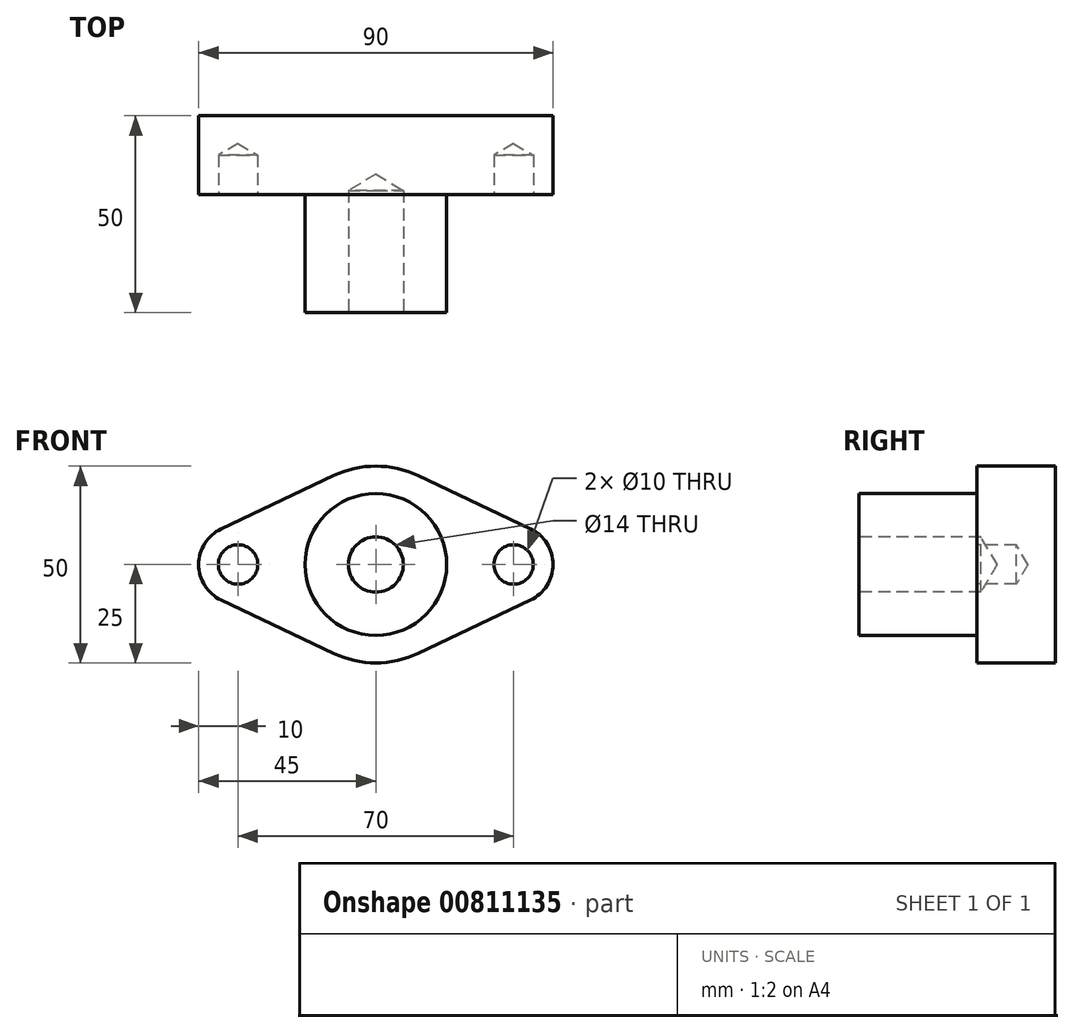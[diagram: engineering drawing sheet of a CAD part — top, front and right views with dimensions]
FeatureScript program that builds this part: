
annotation { "Feature Type Name" : "Feature", "Feature Type Description" : "" }
export const myFeature = defineFeature(function(context is Context, id is Id, definition is map)
    precondition{}
    {
        {
            var Q0;
            Q0=qCreatedBy(makeId("Front.planeOp"),FACE);
            var sketch = newSketch(context, id + "F0", { "sketchPlane" : qUnion([Q0])});
            skCircle(sketch, "E0", {"center": v(0, 0) * mm, "radius": 25 * mm});
            skPoint(sketch, "E1", {"position": v(-35, 0) * mm});
            skPoint(sketch, "E2", {"position": v(35, 0) * mm});
            skCircle(sketch, "E3", {"center": v(-35, 0) * mm, "radius": 10 * mm});
            skCircle(sketch, "E4", {"center": v(35, 0) * mm, "radius": 10 * mm});
            skLineSegment(sketch, "E5", {"start": v(-58.33, 0) * mm, "end": v(0, 27.67) * mm});
            skLineSegment(sketch, "E6", {"start": v(-58.33, 0) * mm, "end": v(0, -27.67) * mm});
            skLineSegment(sketch, "E7", {"start": v(58.33, 0) * mm, "end": v(0, -27.67) * mm});
            skLineSegment(sketch, "E8", {"start": v(0, 27.67) * mm, "end": v(58.33, 0) * mm});
            skSolve(sketch);
        }
        {
            var Q0;
            {var subQ0=sQuery(id+"F0.wireOp",EDGE,"E0");var subQ4=makeQuery(id+"F0.imprint","INTERSECT",VERTEX,{"derivedFrom":[subQ0,sQuery(id+"F0.wireOp",EDGE,"E8")]});Q0=makeQuery(id+"F0.imprint","IMPRINT",FACE,{"disambiguationData":[TD([[makeQuery(id+"F0.imprint","IMPRINT",EDGE,{"disambiguationData":[TD([[subQ4,1.0]])],"derivedFrom":subQ0}),1.0]])]});}
            var Q1;
            {var subQ0=sQuery(id+"F0.wireOp",EDGE,"E5");var subQ1=sQuery(id+"F0.wireOp",EDGE,"E3");var subQ2=makeQuery(id+"F0.imprint","INTERSECT",VERTEX,{"derivedFrom":[subQ1,subQ0]});Q1=makeQuery(id+"F0.imprint","IMPRINT",FACE,{"disambiguationData":[TD([[makeQuery(id+"F0.imprint","IMPRINT",EDGE,{"disambiguationData":[TD([[subQ2,-1.0]])],"derivedFrom":subQ1}),-1.0]])]});}
            var Q2;
            {var subQ0=sQuery(id+"F0.wireOp",EDGE,"E5");var subQ1=sQuery(id+"F0.wireOp",EDGE,"E0");var subQ2=makeQuery(id+"F0.imprint","INTERSECT",VERTEX,{"derivedFrom":[subQ1,subQ0]});Q2=makeQuery(id+"F0.imprint","IMPRINT",FACE,{"disambiguationData":[TD([[makeQuery(id+"F0.imprint","IMPRINT",EDGE,{"disambiguationData":[TD([[subQ2,-1.0]])],"derivedFrom":subQ1}),-1.0]])]});}
            var Q3;
            {var subQ0=sQuery(id+"F0.wireOp",EDGE,"E6");var subQ1=sQuery(id+"F0.wireOp",EDGE,"E0");var subQ2=makeQuery(id+"F0.imprint","INTERSECT",VERTEX,{"derivedFrom":[subQ1,subQ0]});Q3=makeQuery(id+"F0.imprint","IMPRINT",FACE,{"disambiguationData":[TD([[makeQuery(id+"F0.imprint","IMPRINT",EDGE,{"disambiguationData":[TD([[subQ2,1.0]])],"derivedFrom":subQ1}),-1.0]])]});}
            var Q4;
            {var subQ0=sQuery(id+"F0.wireOp",EDGE,"E3");var subQ1=makeQuery(id+"F0.imprint","INTERSECT",VERTEX,{"derivedFrom":[subQ0,sQuery(id+"F0.wireOp",EDGE,"E5")]});Q4=makeQuery(id+"F0.imprint","IMPRINT",FACE,{"disambiguationData":[TD([[makeQuery(id+"F0.imprint","IMPRINT",EDGE,{"disambiguationData":[TD([[subQ1,1.0]])],"derivedFrom":subQ0}),1.0]])]});}
            var Q5;
            {var subQ0=sQuery(id+"F0.wireOp",EDGE,"E6");var subQ1=sQuery(id+"F0.wireOp",EDGE,"E0");var subQ2=makeQuery(id+"F0.imprint","INTERSECT",VERTEX,{"derivedFrom":[subQ1,subQ0]});Q5=makeQuery(id+"F0.imprint","IMPRINT",FACE,{"disambiguationData":[TD([[makeQuery(id+"F0.imprint","IMPRINT",EDGE,{"disambiguationData":[TD([[subQ2,-1.0]])],"derivedFrom":subQ1}),-1.0]])]});}
            var Q6;
            {var subQ0=sQuery(id+"F0.wireOp",EDGE,"E8");var subQ1=sQuery(id+"F0.wireOp",EDGE,"E0");var subQ2=makeQuery(id+"F0.imprint","INTERSECT",VERTEX,{"derivedFrom":[subQ1,subQ0]});Q6=makeQuery(id+"F0.imprint","IMPRINT",FACE,{"disambiguationData":[TD([[makeQuery(id+"F0.imprint","IMPRINT",EDGE,{"disambiguationData":[TD([[subQ2,-1.0]])],"derivedFrom":subQ1}),-1.0]])]});}
            var Q7;
            {var subQ0=sQuery(id+"F0.wireOp",EDGE,"E8");var subQ1=sQuery(id+"F0.wireOp",EDGE,"E4");var subQ2=makeQuery(id+"F0.imprint","INTERSECT",VERTEX,{"derivedFrom":[subQ1,subQ0]});Q7=makeQuery(id+"F0.imprint","IMPRINT",FACE,{"disambiguationData":[TD([[makeQuery(id+"F0.imprint","IMPRINT",EDGE,{"disambiguationData":[TD([[subQ2,1.0]])],"derivedFrom":subQ1}),-1.0]])]});}
            var Q8;
            {var subQ0=sQuery(id+"F0.wireOp",EDGE,"E8");var subQ1=sQuery(id+"F0.wireOp",EDGE,"E0");var subQ2=makeQuery(id+"F0.imprint","INTERSECT",VERTEX,{"derivedFrom":[subQ1,subQ0]});Q8=makeQuery(id+"F0.imprint","IMPRINT",FACE,{"disambiguationData":[TD([[makeQuery(id+"F0.imprint","IMPRINT",EDGE,{"disambiguationData":[TD([[subQ2,1.0]])],"derivedFrom":subQ1}),-1.0]])]});}
            var Q9;
            {var subQ0=sQuery(id+"F0.wireOp",EDGE,"E7");var subQ1=sQuery(id+"F0.wireOp",EDGE,"E0");var subQ2=makeQuery(id+"F0.imprint","INTERSECT",VERTEX,{"derivedFrom":[subQ1,subQ0]});Q9=makeQuery(id+"F0.imprint","IMPRINT",FACE,{"disambiguationData":[TD([[makeQuery(id+"F0.imprint","IMPRINT",EDGE,{"disambiguationData":[TD([[subQ2,-1.0]])],"derivedFrom":subQ1}),-1.0]])]});}
            var Q10;
            {var subQ0=sQuery(id+"F0.wireOp",EDGE,"E4");var subQ1=makeQuery(id+"F0.imprint","INTERSECT",VERTEX,{"derivedFrom":[subQ0,sQuery(id+"F0.wireOp",EDGE,"E8")]});Q10=makeQuery(id+"F0.imprint","IMPRINT",FACE,{"disambiguationData":[TD([[makeQuery(id+"F0.imprint","IMPRINT",EDGE,{"disambiguationData":[TD([[subQ1,-1.0]])],"derivedFrom":subQ0}),1.0]])]});}
            extrude(context, id + "F1", {"entities" : qUnion([Q0, Q1, Q2, Q3, Q4, Q5, Q6, Q7, Q8, Q9, Q10]), "oppositeDirection" : true, "depth" : 20 * mm, "offsetDistance" : 25 * mm});
        }
        {
            var Q0;
            Q0=makeQuery(id+"F1.opExtrude","SWEPT_EDGE",EDGE,{"disambiguationData":[OSD([sQuery(id+"F0.wireOp",EDGE,"E5"),sQuery(id+"F0.wireOp",EDGE,"E6")])]});
            var Q1;
            Q1=makeQuery(id+"F1.opExtrude","SWEPT_EDGE",EDGE,{"disambiguationData":[OSD([sQuery(id+"F0.wireOp",EDGE,"E7"),sQuery(id+"F0.wireOp",EDGE,"E8")])]});
            fillet(context, id + "F2", {"entities" : qUnion([Q0, Q1]), "radius" : 10 * mm, "tangentPropagation" : true, "allowEdgeOverflow" : false});
        }
        {
            var Q0;
            Q0=sQuery(id+"F0.wireOp",VERTEX,"E1");
            var Q1;
            Q1=sQuery(id+"F0.wireOp",VERTEX,"E2");
            var Q2;
            Q2=makeQuery(id+"F1.opExtrude","SWEPT_BODY",BODY,{"disambiguationData":[OSD([sQuery(id+"F0.wireOp",EDGE,"E5"),sQuery(id+"F0.wireOp",EDGE,"E6"),sQuery(id+"F0.wireOp",EDGE,"E7"),sQuery(id+"F0.wireOp",EDGE,"E8")])]});
            hole(context, id + "F3", {"style" : HoleStyle.SIMPLE, "endStyle" : HoleEndStyle.BLIND, "holeDiameter" : 10 * mm, "majorDiameter" : 5 * mm, "holeDepth" : 10 * mm, "isTappedThrough" : true, "tappedDepth" : 12 * mm, "tapClearance" : 3, "locations" : qUnion([Q0, Q1]), "scope" : qUnion([Q2])});
        }
        {
            var Q0;
            {var subQ0=sQuery(id+"F0.wireOp",EDGE,"E0");var subQ4=makeQuery(id+"F0.imprint","INTERSECT",VERTEX,{"derivedFrom":[subQ0,sQuery(id+"F0.wireOp",EDGE,"E8")]});Q0=makeQuery(id+"F0.imprint","IMPRINT",FACE,{"disambiguationData":[TD([[makeQuery(id+"F0.imprint","IMPRINT",EDGE,{"disambiguationData":[TD([[subQ4,1.0]])],"derivedFrom":subQ0}),1.0]])]});}
            var sketch = newSketch(context, id + "F4", { "sketchPlane" : qUnion([Q0])});
            skCircle(sketch, "E9", {"center": v(0, 0) * mm, "radius": 18 * mm});
            skSolve(sketch);
        }
        {
            var Q0;
            Q0=makeQuery(id+"F4.imprint","IMPRINT",FACE,{"disambiguationData":[TD([[makeQuery(id+"F4.imprint","IMPRINT",EDGE,{"derivedFrom":sQuery(id+"F4.wireOp",EDGE,"E9")}),1.0]])]});
            extrude(context, id + "F5", {"entities" : qUnion([Q0]), "operationType" : NewBodyOperationType.ADD, "depth" : 30 * mm, "offsetDistance" : 25 * mm});
        }
        {
            var Q0;
            Q0=makeQuery(id+"F5.opExtrude","CAP_FACE",FACE,{"disambiguationData":[OSD([sQuery(id+"F4.wireOp",EDGE,"E9")])],"isStart":false});
            var sketch = newSketch(context, id + "F6", { "sketchPlane" : qUnion([Q0])});
            skPoint(sketch, "E10", {"position": v(0, 0) * mm});
            skSolve(sketch);
        }
        {
            var Q0;
            Q0=sQuery(id+"F6.wireOp",VERTEX,"E10");
            var Q1;
            Q1=makeQuery(id+"F1.opExtrude","SWEPT_BODY",BODY,{"disambiguationData":[OSD([sQuery(id+"F0.wireOp",EDGE,"E5"),sQuery(id+"F0.wireOp",EDGE,"E6"),sQuery(id+"F0.wireOp",EDGE,"E7"),sQuery(id+"F0.wireOp",EDGE,"E8")])]});
            hole(context, id + "F7", {"style" : HoleStyle.SIMPLE, "endStyle" : HoleEndStyle.BLIND, "standardTappedOrClearance" : lookupTablePath({ "standard" : "ISO", "engagement" : "75%", "pitch" : "2 mm", "size" : "M16", "type" : "Tapped" }), "standardBlindInLast" : lookupTablePath({ "standard" : "ISO", "engagement" : "75%", "pitch" : "2 mm", "size" : "M16", "type" : "Tapped" }), "holeDiameter" : 14 * mm, "majorDiameter" : 16 * mm, "showTappedDepth" : true, "holeDepth" : 31 * mm, "isTappedThrough" : true, "tappedDepth" : 25 * mm, "tapClearance" : 3, "locations" : qUnion([Q0]), "scope" : qUnion([Q1])});
        }
        {
            var Q0;
            Q0=makeQuery(id+"F1.opExtrude","SWEPT_EDGE",EDGE,{"disambiguationData":[OSD([sQuery(id+"F0.wireOp",EDGE,"E5"),sQuery(id+"F0.wireOp",EDGE,"E8")])]});
            var Q1;
            Q1=makeQuery(id+"F1.opExtrude","SWEPT_EDGE",EDGE,{"disambiguationData":[OSD([sQuery(id+"F0.wireOp",EDGE,"E6"),sQuery(id+"F0.wireOp",EDGE,"E7")])]});
            fillet(context, id + "F8", {"entities" : qUnion([Q0, Q1]), "radius" : 25 * mm, "tangentPropagation" : true, "allowEdgeOverflow" : false});
        }
    });
